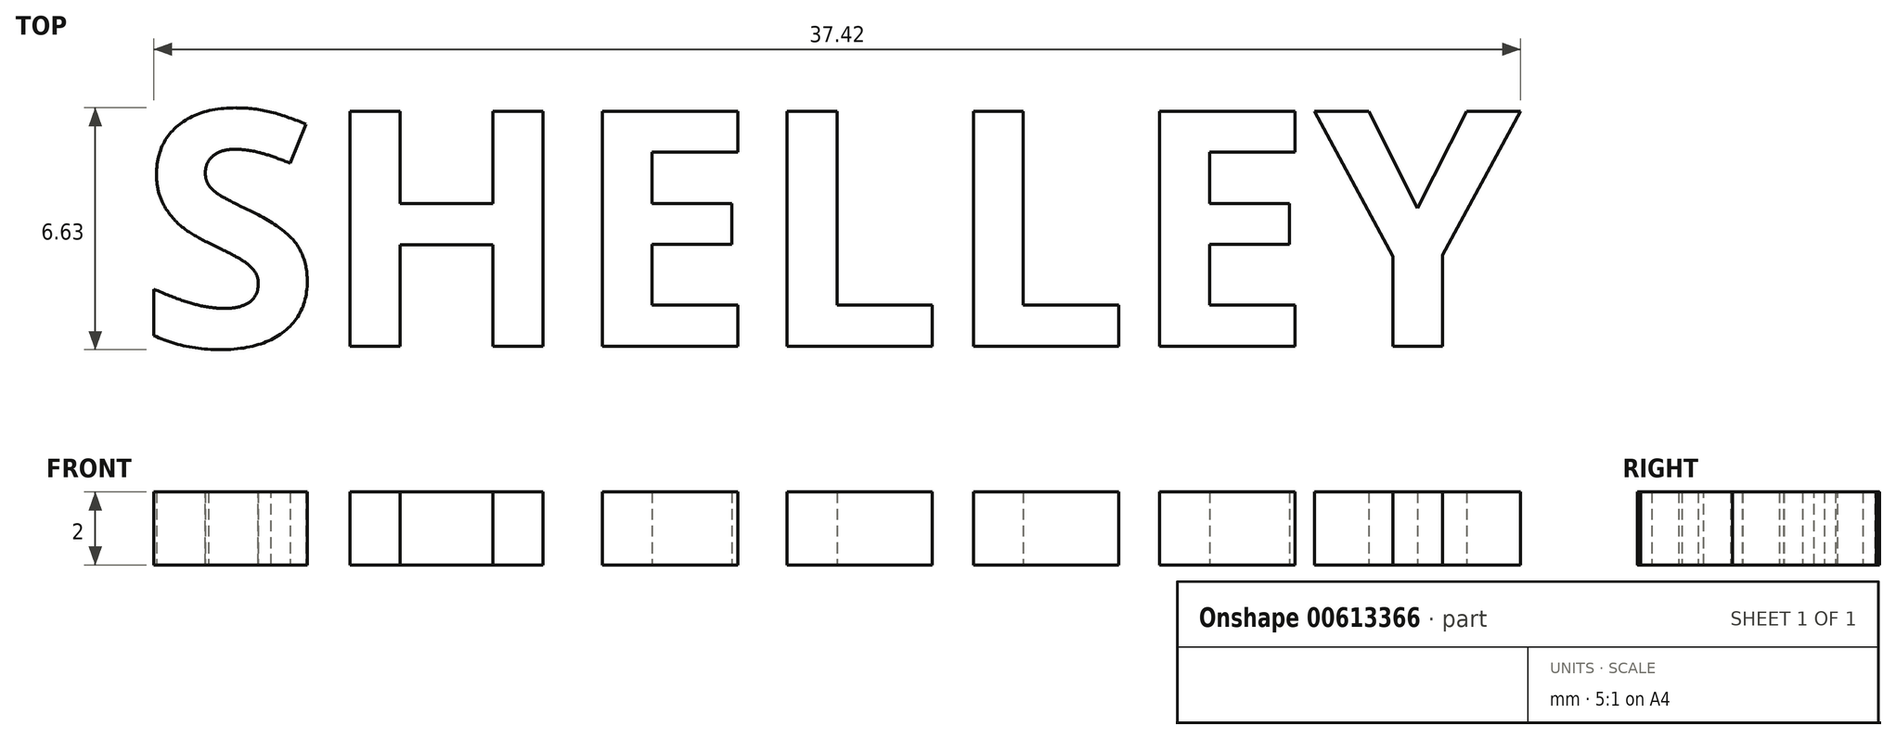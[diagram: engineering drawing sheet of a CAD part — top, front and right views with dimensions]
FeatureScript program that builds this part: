
annotation { "Feature Type Name" : "Feature", "Feature Type Description" : "" }
export const myFeature = defineFeature(function(context is Context, id is Id, definition is map)
    precondition{}
    {
        {
            var Q0;
            Q0=qCreatedBy(makeId("Top.planeOp"),FACE);
            var sketch = newSketch(context, id + "F0", { "sketchPlane" : qUnion([Q0])});
            skText(sketch, "E0", { "text": "SHELLEY", "fontName": "OpenSans-Bold.ttf"});
            skPoint(sketch, "E1", {"position": v(0.18, 8.09) * mm});
            skPoint(sketch, "E2", {"position": v(-49.62, 5.9) * mm});
            const initialGuessF0  = {"E0": [-0.04653, -0.00082, 1, 0, 0.0065]};
            skSetInitialGuess(sketch, initialGuessF0);
            skSolve(sketch);
        }
        {
            var Q0;
            Q0=makeQuery(id+"F0.imprint","IMPRINT",FACE,{"disambiguationData":[TD([[makeQuery(id+"F0.imprint","IMPRINT",EDGE,{"derivedFrom":sQuery(id+"F0.wireOp",EDGE,"E0.sketch_text.stroke-0")}),-1.0]])]});
            var Q1;
            Q1=makeQuery(id+"F0.imprint","IMPRINT",FACE,{"disambiguationData":[TD([[makeQuery(id+"F0.imprint","IMPRINT",EDGE,{"derivedFrom":sQuery(id+"F0.wireOp",EDGE,"E0.sketch_text.stroke-28")}),-1.0]])]});
            var Q2;
            Q2=makeQuery(id+"F0.imprint","IMPRINT",FACE,{"disambiguationData":[TD([[makeQuery(id+"F0.imprint","IMPRINT",EDGE,{"derivedFrom":sQuery(id+"F0.wireOp",EDGE,"E0.sketch_text.stroke-40")}),-1.0]])]});
            var Q3;
            Q3=makeQuery(id+"F0.imprint","IMPRINT",FACE,{"disambiguationData":[TD([[makeQuery(id+"F0.imprint","IMPRINT",EDGE,{"derivedFrom":sQuery(id+"F0.wireOp",EDGE,"E0.sketch_text.stroke-52")}),-1.0]])]});
            var Q4;
            Q4=makeQuery(id+"F0.imprint","IMPRINT",FACE,{"disambiguationData":[TD([[makeQuery(id+"F0.imprint","IMPRINT",EDGE,{"derivedFrom":sQuery(id+"F0.wireOp",EDGE,"E0.sketch_text.stroke-58")}),-1.0]])]});
            var Q5;
            Q5=makeQuery(id+"F0.imprint","IMPRINT",FACE,{"disambiguationData":[TD([[makeQuery(id+"F0.imprint","IMPRINT",EDGE,{"derivedFrom":sQuery(id+"F0.wireOp",EDGE,"E0.sketch_text.stroke-64")}),-1.0]])]});
            var Q6;
            Q6=makeQuery(id+"F0.imprint","IMPRINT",FACE,{"disambiguationData":[TD([[makeQuery(id+"F0.imprint","IMPRINT",EDGE,{"derivedFrom":sQuery(id+"F0.wireOp",EDGE,"E0.sketch_text.stroke-76")}),-1.0]])]});
            extrude(context, id + "F1", {"entities" : qUnion([Q0, Q1, Q2, Q3, Q4, Q5, Q6]), "depth" : 2 * mm, "offsetDistance" : 25 * mm});
        }
    });
